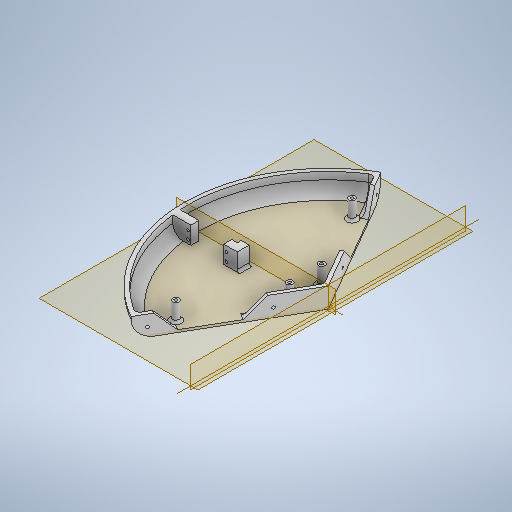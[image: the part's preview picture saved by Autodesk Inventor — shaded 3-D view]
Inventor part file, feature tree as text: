
AUTODESK INVENTOR PART (.ipt)
format: ipt  version: 2025.1 (Build 291241000, 241)  size: 560,128 bytes
history: native  units: mm
features: extrude x12, sketch x12, fillet x7
ambient origin geometry x8: Origin, YZ Plane, XZ Plane, XY Plane, X Axis, Y Axis, Z Axis, Center Point
bodies: Solid1 (feature_tree)
feature tree (31):
  extrude  "Extrusion1"  TaperAngle=60.0deg  [1 undecoded]
  extrude  "Extrusion2"  Depth=22.0mm TaperAngle=0.0deg
  extrude  "Extrusion4"  TaperAngle=0.0deg  [1 undecoded]
  extrude  "Extrusion5"  Depth=50.0mm
  extrude  "Extrusion8"  Depth=3.3mm
  extrude  "Extrusion9"  Depth=50.0mm
  extrude  "Extrusion10"  Depth=3.0mm TaperAngle=0.0deg
  fillet  "Rundung2"  Radius=9.8mm
  fillet  "Rundung3"  Radius=55.0mm
  extrude  "Extrusion11"  Depth=110.5mm
  extrude  "Extrusion12"  Depth=5.0mm
  fillet  "Rundung4"  Radius=3.0mm
  fillet  "Rundung5"  Radius=5.0mm
  extrude  "Extrusion13"  TaperAngle=0.0deg  [1 undecoded]
  extrude  "Extrusion14"  Depth=10.0mm TaperAngle=0.0deg
  fillet  "Rundung6"  Radius=350.0mm
  fillet  "Rundung7"  [1 undecoded]
  extrude  "Extrusion15"  Depth=10.0mm
  fillet  "Rundung8"  Radius=10.0mm
  sketch  "Sketch1"  dims[d3=180.0mm d4=60.0deg]
  sketch  "Sketch4"  dims[d5=120.0deg d7=22.0mm d8=0.0mm]
  sketch  "Sketch8"  dims[d43=160.0mm d47=0.0mm d48=0.0mm]
  sketch  "Sketch9"  dims[d68=3.3mm d70=50.0mm]
  sketch  "Sketch12"  dims[d72=15.0mm d73=0.0mm d74=3.3mm]
  sketch  "Skizze13"  dims[d75=3.3mm d76=50.0mm]
  sketch  "Skizze15"  dims[d78=15.0mm d79=0.0mm d93=3.0mm d94=0.0mm d98=9.8mm d99=55.0mm]
  sketch  "Skizze16"  dims[d101=41.0mm d102=110.5mm]
  sketch  "Skizze17"  dims[d103=120.0deg d104=41.0mm d105=3.0mm d106=5.0mm]
  sketch  "Skizze19"  dims[d109=-2.0mm d110=0.0mm]
  sketch  "Skizze22"  dims[d111=10.0mm d112=22.0mm d113=0.0mm d115=350.0mm d116=120.0deg]
  sketch  "Skizze23"  dims[d117=10.0mm d118=10.0mm d119=10.0mm d120=22.0mm d121=0.0mm d122=13.0mm d123=22.0mm d127=10.0mm d128=8.0mm d129=8.0mm d130=10.0mm d131=90.0mm d132=20.0mm d133=8.0mm d134=8.0mm d135=90.0mm d136=20.0mm d137=10.0mm d138=10.0mm d139=22.0mm d140=0.0mm d141=3.6mm d142=5.0mm d143=0.0mm d144=3.0mm d145=3.0mm d146=10.0mm d147=10.0mm d148=3.3mm d149=3.3mm d150=3.3mm d151=3.3mm d153=3.4mm d154=3.4mm d155=3.4mm d156=3.4mm d157=4.8mm d158=4.8mm d159=5.0mm d160=0.0mm d161=115.0mm d164=115.0mm d165=45.0deg d166=45.0deg d167=60.0mm d168=57.5mm d169=0.0mm d170=0.0mm d171=5.0mm d172=0.0mm d173=5.0mm d174=5.0mm d175=8.0mm d176=8.0mm d177=8.0mm d178=8.0mm d179=45.0deg d180=45.0deg d181=57.5mm d182=5.0mm d183=0.0mm d184=60.0mm d185=0.0mm d186=5.0mm d54=1.0mm d55=1.0mm d56=1.0mm d57=0.15mm d58=0.25mm d59=0.375mm d60=14.3117mm d61=0.75mm d62=20.594885mm d63=0.0625mm d64=0.75mm d65=0.375mm d85=0.5mm d86=0.872665mm d87=0.5mm d88=0.872665mm d96=0.5mm d97=0.872665mm]
note: 4 required parameter values undecoded (feature->parameter linkage not recoverable at this tier; creation-order binding heuristic only, values carry confidence <= 0.55)
